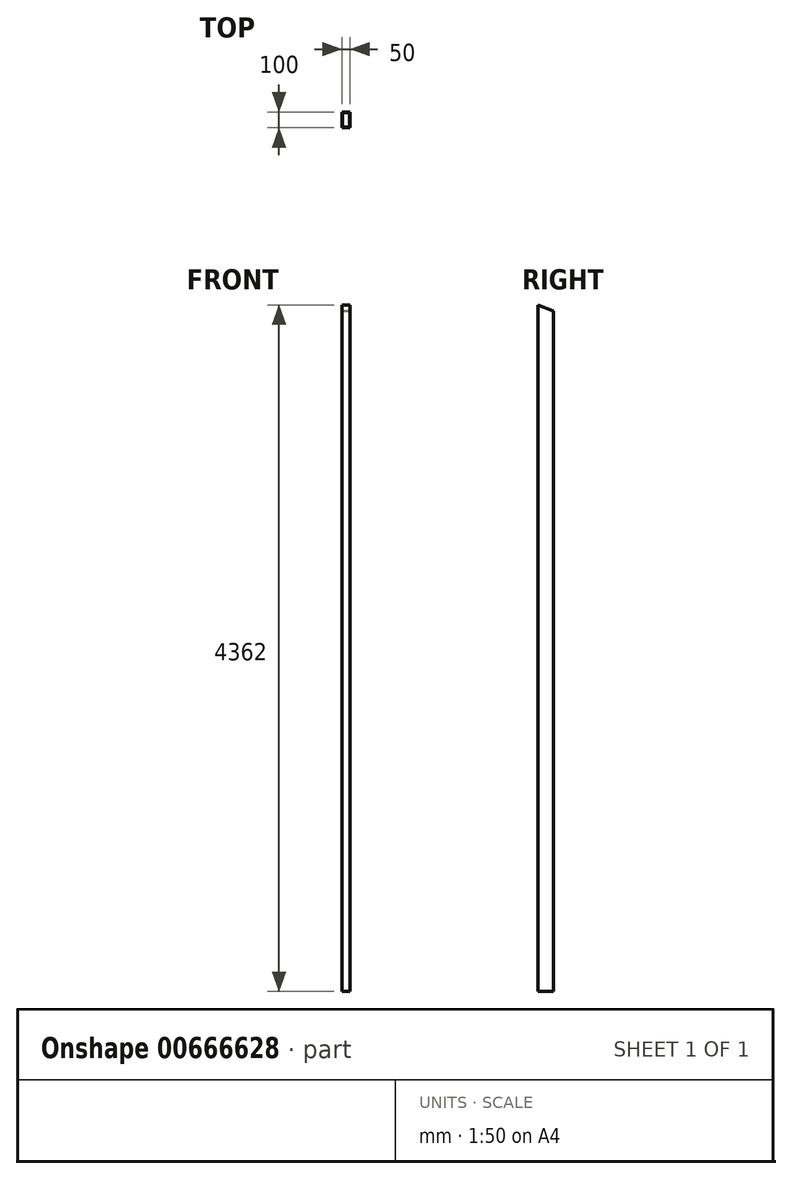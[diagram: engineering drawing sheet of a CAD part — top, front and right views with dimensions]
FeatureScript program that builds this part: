
annotation { "Feature Type Name" : "Feature", "Feature Type Description" : "" }
export const myFeature = defineFeature(function(context is Context, id is Id, definition is map)
    precondition{}
    {
        {
            var Q0;
            Q0=qCreatedBy(makeId("Top.planeOp"),FACE);
            var sketch = newSketch(context, id + "F0", { "sketchPlane" : qUnion([Q0])});
            skPoint(sketch, "E0.middle", {"position": v(0, 0) * mm});
            skLineSegment(sketch, "E1.bottom", {"start": v(25, -50) * mm, "end": v(-25, -50) * mm});
            skLineSegment(sketch, "E1.top", {"start": v(25, 50) * mm, "end": v(-25, 50) * mm});
            skLineSegment(sketch, "E1.left", {"start": v(25, -50) * mm, "end": v(25, 50) * mm});
            skLineSegment(sketch, "E1.right", {"start": v(-25, -50) * mm, "end": v(-25, 50) * mm});
            skLineSegment(sketch, "E2.bottom", {"start": v(22, -47) * mm, "end": v(-22, -47) * mm});
            skLineSegment(sketch, "E2.top", {"start": v(22, 47) * mm, "end": v(-22, 47) * mm});
            skLineSegment(sketch, "E2.left", {"start": v(22, -47) * mm, "end": v(22, 47) * mm});
            skLineSegment(sketch, "E2.right", {"start": v(-22, -47) * mm, "end": v(-22, 47) * mm});
            skSolve(sketch);
        }
        {
            var Q0;
            Q0=makeQuery(id+"F0.imprint","IMPRINT",FACE,{"disambiguationData":[TD([[makeQuery(id+"F0.imprint","IMPRINT",EDGE,{"derivedFrom":sQuery(id+"F0.wireOp",EDGE,"E1.bottom")}),-1.0]])]});
            extrude(context, id + "F1", {"entities" : qUnion([Q0]), "depth" : 4362 * mm, "offsetDistance" : 25 * mm});
        }
        {
            var Q0;
            Q0=makeQuery(id+"F1.opExtrude","CAP_EDGE",EDGE,{"disambiguationData":[OSD([sQuery(id+"F0.wireOp",EDGE,"E1.top")])],"isStart":false});
            chamfer(context, id + "F2", {"entities" : qUnion([Q0]), "chamferType" : ChamferType.TWO_OFFSETS, "width1" : 100 * mm, "oppositeDirection" : false, "width2" : 41 * mm, "tangentPropagation" : true});
        }
    });
